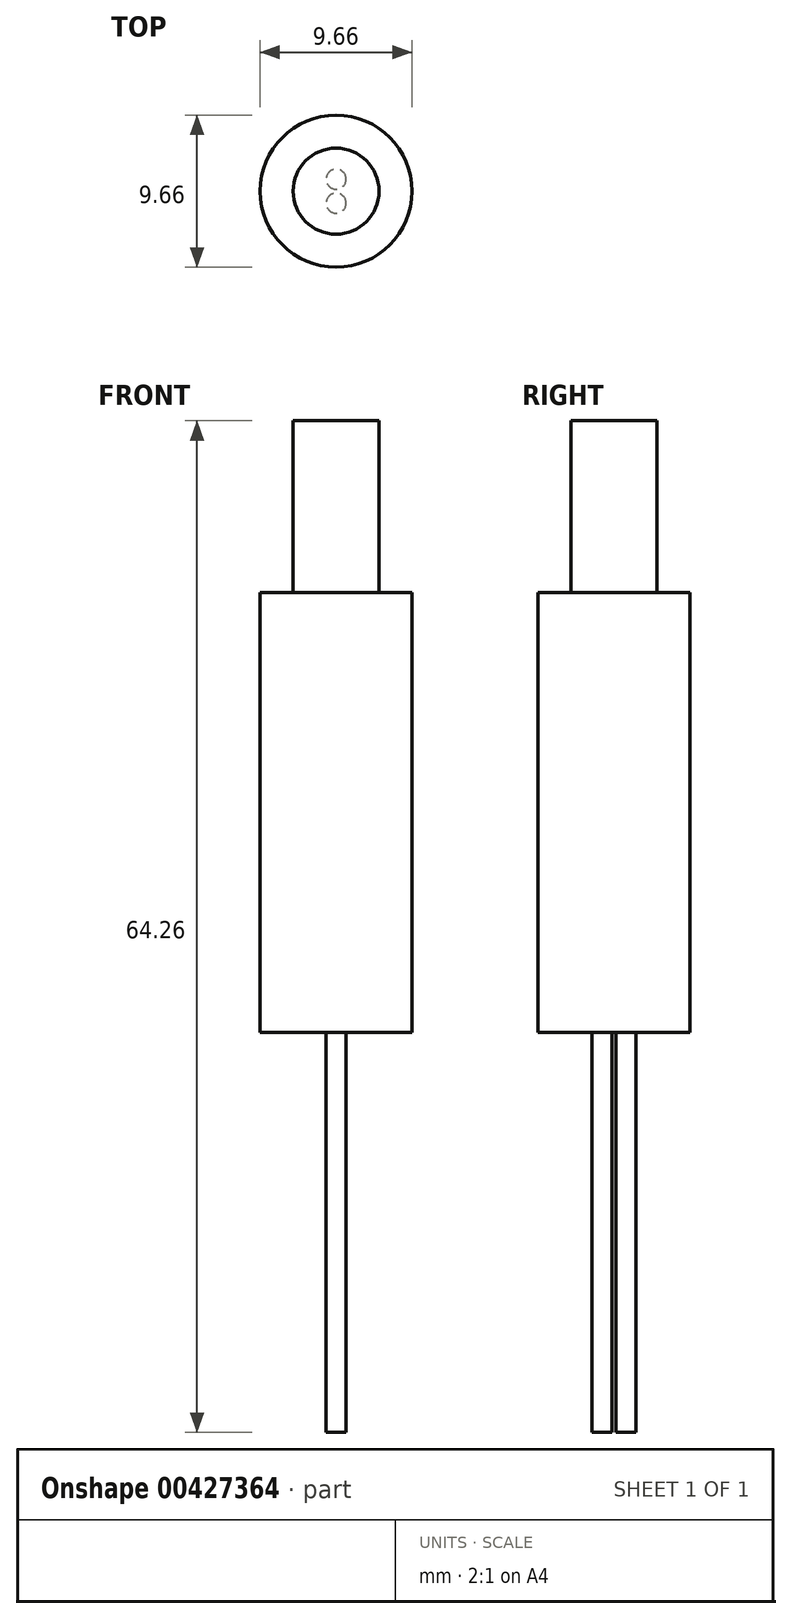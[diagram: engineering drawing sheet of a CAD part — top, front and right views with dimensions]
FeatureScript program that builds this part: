
annotation { "Feature Type Name" : "Feature", "Feature Type Description" : "" }
export const myFeature = defineFeature(function(context is Context, id is Id, definition is map)
    precondition{}
    {
        {
            var Q0;
            Q0=qCreatedBy(makeId("Top.planeOp"),FACE);
            var sketch = newSketch(context, id + "F0", { "sketchPlane" : qUnion([Q0])});
            skCircle(sketch, "E0", {"center": v(0, 0) * mm, "radius": 2.73 * mm});
            skCircle(sketch, "E1", {"center": v(0, 0) * mm, "radius": 4.83 * mm});
            skSolve(sketch);
        }
        {
            var Q0;
            Q0=makeQuery(id+"F0.imprint","IMPRINT",FACE,{"disambiguationData":[TD([[makeQuery(id+"F0.imprint","IMPRINT",EDGE,{"derivedFrom":sQuery(id+"F0.wireOp",EDGE,"E0")}),1.0]])]});
            extrude(context, id + "F1", {"entities" : qUnion([Q0]), "depth" : 10.92 * mm, "offsetDistance" : 25.4 * mm});
        }
        {
            var Q0;
            Q0 = qSketchRegion(id + "F0", true);
            var Q1;
            Q1=makeQuery(id+"F0.imprint","IMPRINT",FACE,{"disambiguationData":[TD([[makeQuery(id+"F0.imprint","IMPRINT",EDGE,{"derivedFrom":sQuery(id+"F0.wireOp",EDGE,"E0")}),1.0]])]});
            extrude(context, id + "F2", {"entities" : qUnion([Q0, Q1]), "operationType" : NewBodyOperationType.ADD, "oppositeDirection" : true, "depth" : 27.94 * mm, "offsetDistance" : 25.4 * mm});
        }
        {
            var Q0;
            Q0=makeQuery(id+"F2.opExtrude","CAP_FACE",FACE,{"disambiguationData":[OSD([sQuery(id+"F0.wireOp",EDGE,"E1")])],"isStart":false});
            var sketch = newSketch(context, id + "F3", { "sketchPlane" : qUnion([Q0])});
            skLineSegment(sketch, "E2", {"start": v(4.83, 0) * mm, "end": v(-4.83, 0) * mm, "construction": true});
            skCircle(sketch, "E3", {"center": v(0, -0.76) * mm, "radius": 0.64 * mm});
            skPoint(sketch, "E4", {"position": v(0, 0) * mm});
            skLineSegment(sketch, "E5", {"start": v(0, -0.76) * mm, "end": v(0, 0) * mm, "construction": true});
            skCircle(sketch, "E6.MirrorC", {"center": v(0, 0.76) * mm, "radius": 0.64 * mm});
            skLineSegment(sketch, "E7.MirrorCS", {"start": v(0, 0.76) * mm, "end": v(0, 0) * mm, "construction": true});
            skSolve(sketch);
        }
        {
            var Q0;
            Q0 = qSketchRegion(id + "F3", true);
            extrude(context, id + "F4", {"entities" : qUnion([Q0]), "depth" : 25.4 * mm, "offsetDistance" : 25.4 * mm});
        }
    });
